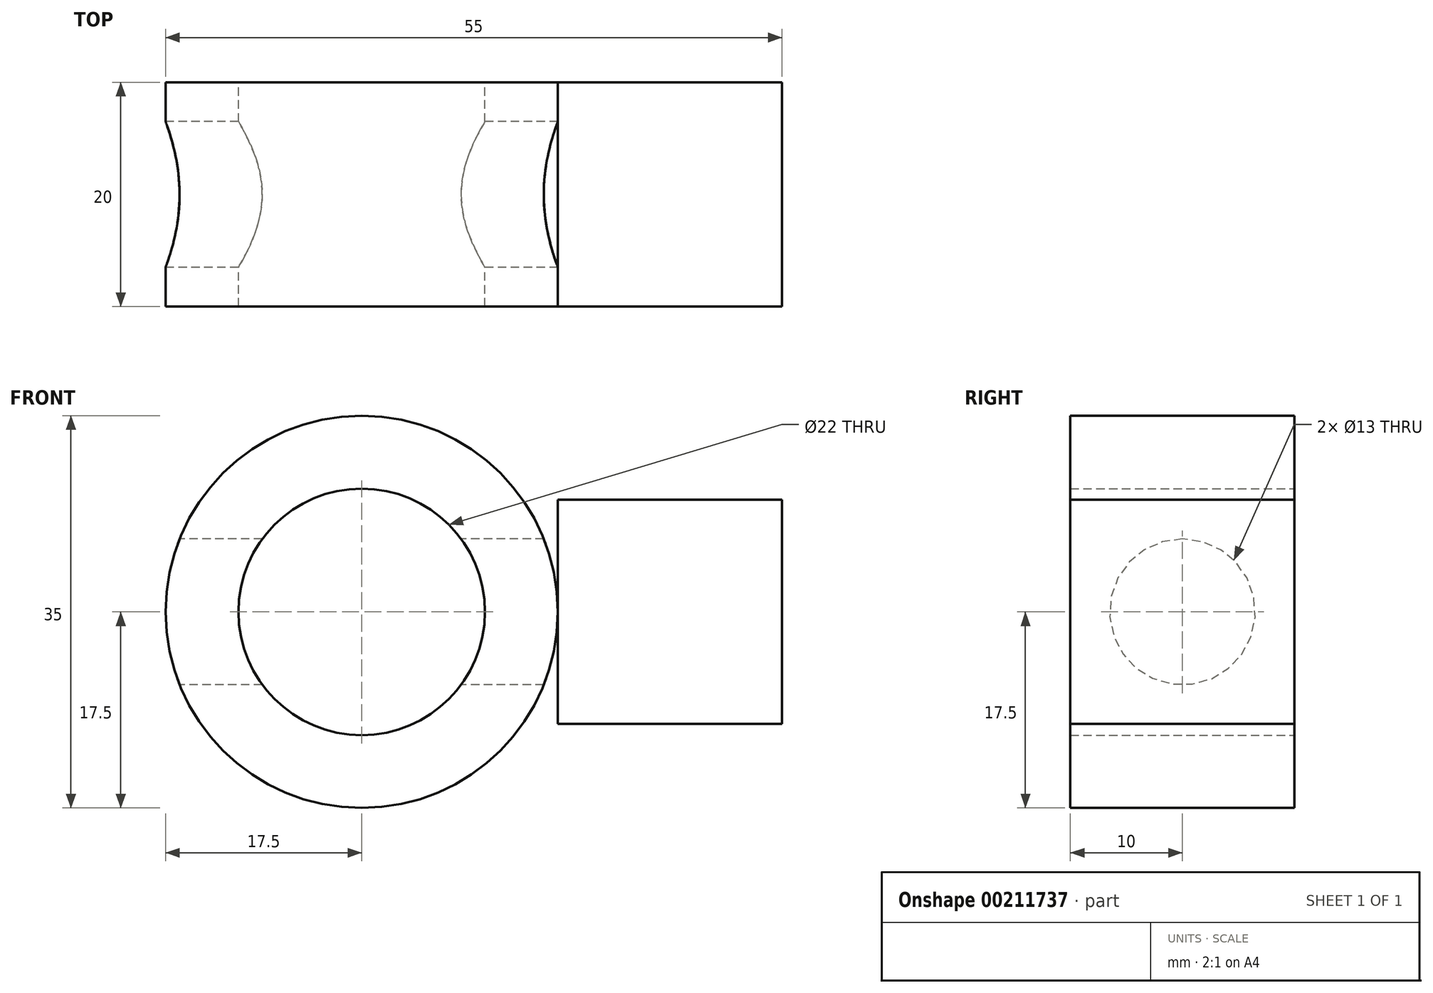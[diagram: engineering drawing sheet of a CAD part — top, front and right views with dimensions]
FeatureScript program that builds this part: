
annotation { "Feature Type Name" : "Feature", "Feature Type Description" : "" }
export const myFeature = defineFeature(function(context is Context, id is Id, definition is map)
    precondition{}
    {
        {
            var Q0;
            Q0=qCreatedBy(makeId("Front.planeOp"),FACE);
            var sketch = newSketch(context, id + "F0", { "sketchPlane" : qUnion([Q0])});
            skLineSegment(sketch, "E0.bottom", {"start": v(10, -10) * mm, "end": v(-10, -10) * mm});
            skLineSegment(sketch, "E0.top", {"start": v(10, 10) * mm, "end": v(-10, 10) * mm});
            skLineSegment(sketch, "E0.left", {"start": v(10, -10) * mm, "end": v(10, 10) * mm});
            skLineSegment(sketch, "E0.right", {"start": v(-10, -10) * mm, "end": v(-10, 10) * mm});
            skPoint(sketch, "E0.middle", {"position": v(0, 0) * mm});
            skLineSegment(sketch, "E1", {"start": v(0, 0) * mm, "end": v(-27.5, 0) * mm});
            skPoint(sketch, "E2", {"position": v(-27.5, 0) * mm});
            skPoint(sketch, "E3", {"position": v(-10, 0) * mm});
            skCircle(sketch, "E4", {"center": v(-27.5, 0) * mm, "radius": 17.5 * mm});
            skCircle(sketch, "E5", {"center": v(-27.5, 0) * mm, "radius": 11 * mm});
            skLineSegment(sketch, "E6", {"start": v(-10, 10) * mm, "end": v(-18.62, 15.08) * mm});
            skLineSegment(sketch, "E7", {"start": v(-10, -10) * mm, "end": v(-18.62, -15.08) * mm});
            skSolve(sketch);
        }
        {
            var Q0;
            Q0=makeQuery(id+"F0.imprint","IMPRINT",FACE,{"disambiguationData":[TD([[makeQuery(id+"F0.imprint","IMPRINT",EDGE,{"derivedFrom":sQuery(id+"F0.wireOp",EDGE,"E5")}),-1.0]])]});
            var Q1;
            {var subQ0=sQuery(id+"F0.wireOp",EDGE,"E6");Q1=makeQuery(id+"F0.imprint","IMPRINT",FACE,{"disambiguationData":[TD([[makeQuery(id+"F0.imprint","IMPRINT",EDGE,{"derivedFrom":subQ0}),1.0]])]});}
            var Q2;
            {var subQ0=sQuery(id+"F0.wireOp",EDGE,"E7");Q2=makeQuery(id+"F0.imprint","IMPRINT",FACE,{"disambiguationData":[TD([[makeQuery(id+"F0.imprint","IMPRINT",EDGE,{"derivedFrom":subQ0}),-1.0]])]});}
            var Q3;
            {var subQ1=sQuery(id+"F0.wireOp",EDGE,"E0.bottom");Q3=makeQuery(id+"F0.imprint","IMPRINT",FACE,{"disambiguationData":[TD([[makeQuery(id+"F0.imprint","IMPRINT",EDGE,{"derivedFrom":subQ1}),-1.0]])]});}
            extrude(context, id + "F1", {"entities" : qUnion([Q0, Q1, Q2, Q3]), "depth" : 20 * mm});
        }
        {
            var Q0;
            Q0=makeQuery(id+"F1.opExtrude","SWEPT_FACE",FACE,{"disambiguationData":[OSD([sQuery(id+"F0.wireOp",EDGE,"E0.left")])]});
            var sketch = newSketch(context, id + "F2", { "sketchPlane" : qUnion([Q0])});
            skSolve(sketch);
        }
        {
            var Q0;
            {var subQ0=sQuery(id+"F0.wireOp",EDGE,"E0.left");Q0=makeQuery(id+"F2.imprint","IMPRINT",FACE,{"disambiguationData":[TD([[makeQuery(id+"F2.imprint","IMPRINT",EDGE,{"derivedFrom":makeQuery(id+"F1.opExtrude","CAP_EDGE",EDGE,{"disambiguationData":[OSD([subQ0])],"isStart":true})}),1.0]])]});}
            cPlane(context, id + "F3", {"entities" : qUnion([Q0]), "cplaneType" : CPlaneType.OFFSET, "offset" : 30 * mm, "oppositeDirection" : true, "width" : 150 * mm, "height" : 150 * mm});
        }
        {
            var Q0;
            Q0=qCreatedBy(id+"F3.planeOp",FACE);
            var sketch = newSketch(context, id + "F4", { "sketchPlane" : qUnion([Q0])});
            skLineSegment(sketch, "E8", {"start": v(0, 0) * mm, "end": v(-20, 0) * mm});
            skPoint(sketch, "E9", {"position": v(-10, 0) * mm});
            skSolve(sketch);
        }
        {
            var Q0;
            Q0=sQuery(id+"F4.wireOp",VERTEX,"E9");
            var Q1;
            Q1=makeQuery(id+"F1.opExtrude","SWEPT_BODY",BODY,{"disambiguationData":[OSD([sQuery(id+"F0.wireOp",EDGE,"E0.bottom"),sQuery(id+"F0.wireOp",EDGE,"E0.top"),sQuery(id+"F0.wireOp",EDGE,"E0.left"),sQuery(id+"F0.wireOp",EDGE,"E4"),sQuery(id+"F0.wireOp",EDGE,"E5"),sQuery(id+"F0.wireOp",EDGE,"E6"),sQuery(id+"F0.wireOp",EDGE,"E7")])]});
            hole(context, id + "F5", {"style" : HoleStyle.C_BORE, "endStyle" : HoleEndStyle.THROUGH, "oppositeDirection" : true, "holeDiameter" : 9 * mm, "cBoreDiameter" : 13 * mm, "cBoreDepth" : 9 * mm, "locations" : qUnion([Q0]), "scope" : qUnion([Q1]), "isTappedThrough" : true});
        }
        {
            var Q0;
            {var subQ0=sQuery(id+"F0.wireOp",EDGE,"E0.left");Q0=makeQuery(id+"F2.imprint","IMPRINT",FACE,{"disambiguationData":[TD([[makeQuery(id+"F2.imprint","IMPRINT",EDGE,{"derivedFrom":makeQuery(id+"F1.opExtrude","CAP_EDGE",EDGE,{"disambiguationData":[OSD([subQ0])],"isStart":true})}),1.0]])]});}
            var sketch = newSketch(context, id + "F6", { "sketchPlane" : qUnion([Q0])});
            skSolve(sketch);
        }
        {
            var Q0;
            {var subQ0=sQuery(id+"F0.wireOp",EDGE,"E0.left");Q0=makeQuery(id+"F6.imprint","IMPRINT",FACE,{"disambiguationData":[TD([[makeQuery(id+"F6.imprint","IMPRINT",EDGE,{"derivedFrom":makeQuery(id+"F2.imprint","IMPRINT",EDGE,{"derivedFrom":makeQuery(id+"F1.opExtrude","CAP_EDGE",EDGE,{"disambiguationData":[OSD([subQ0])],"isStart":true})})}),1.0]])]});}
            cPlane(context, id + "F7", {"entities" : qUnion([Q0]), "cplaneType" : CPlaneType.OFFSET, "offset" : 55 * mm, "oppositeDirection" : true, "width" : 150 * mm, "height" : 150 * mm});
        }
        {
            var Q0;
            Q0=qCreatedBy(id+"F7.planeOp",FACE);
            var sketch = newSketch(context, id + "F8", { "sketchPlane" : qUnion([Q0])});
            skLineSegment(sketch, "E10", {"start": v(0, 0) * mm, "end": v(-20, 0) * mm});
            skPoint(sketch, "E11", {"position": v(-10, 0) * mm});
            skSolve(sketch);
        }
        {
            var Q0;
            Q0=sQuery(id+"F8.wireOp",VERTEX,"E11");
            var Q1;
            Q1=makeQuery(id+"F1.opExtrude","SWEPT_BODY",BODY,{"disambiguationData":[OSD([sQuery(id+"F0.wireOp",EDGE,"E0.bottom"),sQuery(id+"F0.wireOp",EDGE,"E0.top"),sQuery(id+"F0.wireOp",EDGE,"E0.left"),sQuery(id+"F0.wireOp",EDGE,"E4"),sQuery(id+"F0.wireOp",EDGE,"E5"),sQuery(id+"F0.wireOp",EDGE,"E6"),sQuery(id+"F0.wireOp",EDGE,"E7")])]});
            hole(context, id + "F9", {"style" : HoleStyle.SIMPLE, "endStyle" : HoleEndStyle.BLIND, "oppositeDirection" : true, "holeDiameter" : 13 * mm, "holeDepth" : 20 * mm, "locations" : qUnion([Q0]), "scope" : qUnion([Q1])});
        }
    });
